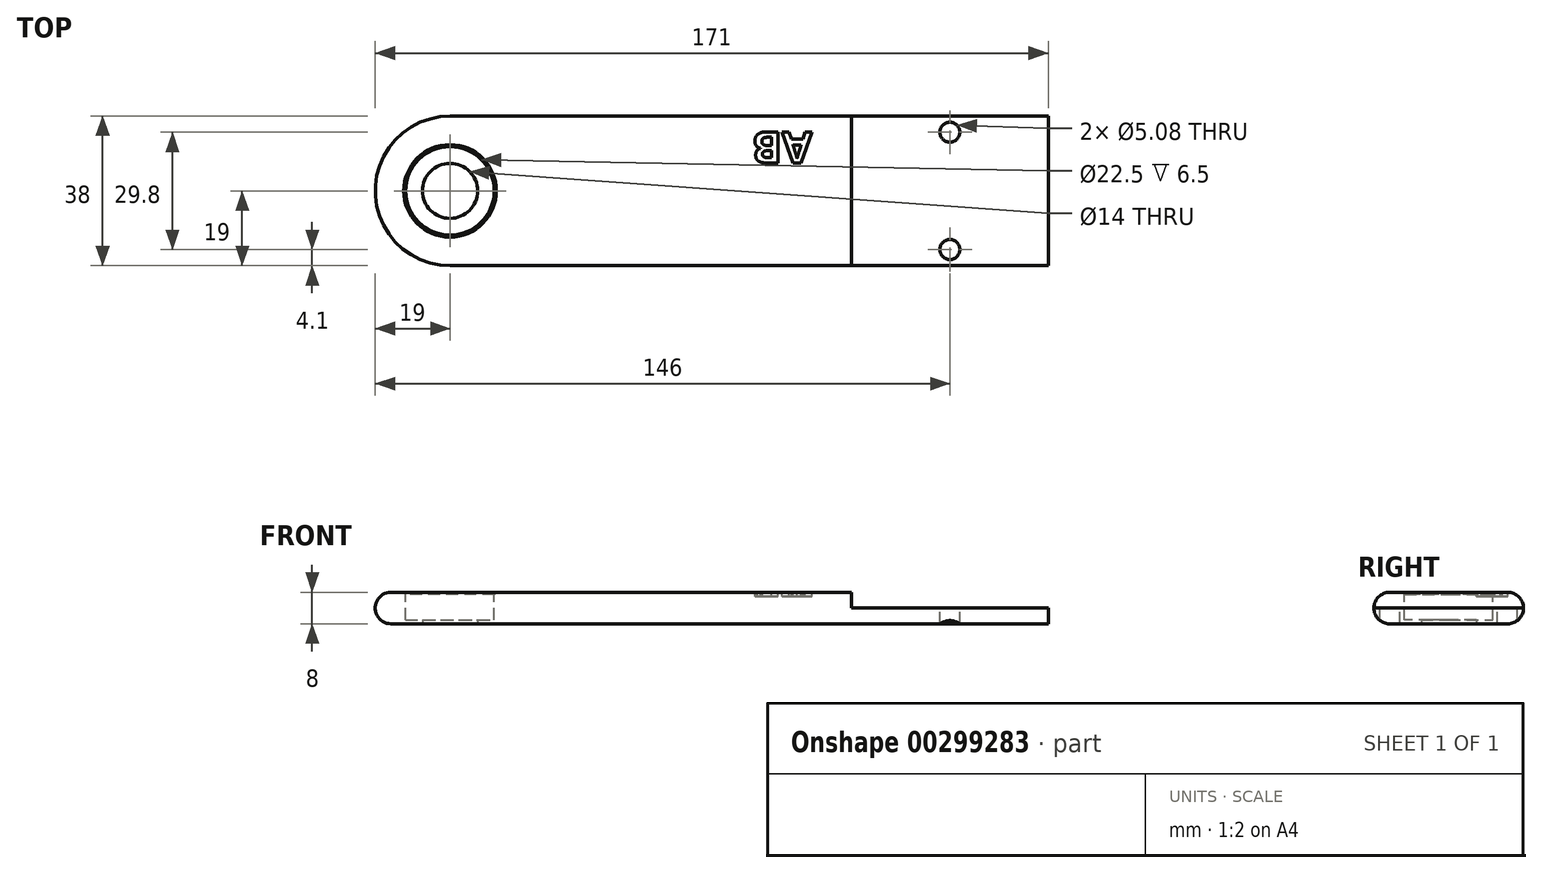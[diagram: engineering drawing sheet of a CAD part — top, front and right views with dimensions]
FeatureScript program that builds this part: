
annotation { "Feature Type Name" : "Feature", "Feature Type Description" : "" }
export const myFeature = defineFeature(function(context is Context, id is Id, definition is map)
    precondition{}
    {
        {
            var Q0;
            Q0=qCreatedBy(makeId("Top.planeOp"),FACE);
            var sketch = newSketch(context, id + "F0", { "sketchPlane" : qUnion([Q0])});
            skArc(sketch, "E0", {"start": v(-127, 19) * mm, "mid": v(-146, 0) * mm, "end": v(-127, -19) * mm});
            skArc(sketch, "E1", {"start": v(127, -19) * mm, "mid": v(146, 0) * mm, "end": v(127, 19) * mm});
            skCircle(sketch, "E2", {"center": v(-127, 0) * mm, "radius": 11.25 * mm});
            skCircle(sketch, "E3", {"center": v(127, 0) * mm, "radius": 11.25 * mm});
            skLineSegment(sketch, "E4", {"start": v(-127, 19) * mm, "end": v(127, 19) * mm});
            skLineSegment(sketch, "E5", {"start": v(-127, -19) * mm, "end": v(127, -19) * mm});
            skSolve(sketch);
        }
        {
            var Q0;
            Q0=makeQuery(id+"F0.imprint","IMPRINT",FACE,{"disambiguationData":[TD([[makeQuery(id+"F0.imprint","IMPRINT",EDGE,{"derivedFrom":sQuery(id+"F0.wireOp",EDGE,"E0")}),1.0]])]});
            var Q1;
            Q1=makeQuery(id+"F0.imprint","IMPRINT",FACE,{"disambiguationData":[TD([[makeQuery(id+"F0.imprint","IMPRINT",EDGE,{"derivedFrom":sQuery(id+"F0.wireOp",EDGE,"E3")}),1.0]])]});
            extrude(context, id + "F1", {"entities" : qUnion([Q0, Q1]), "oppositeDirection" : true, "depth" : 8 * mm});
        }
        {
            var Q0;
            Q0=makeQuery(id+"F1.opExtrude","CAP_FACE",FACE,{"disambiguationData":[OSD([sQuery(id+"F0.wireOp",EDGE,"E0"),sQuery(id+"F0.wireOp",EDGE,"E1"),sQuery(id+"F0.wireOp",EDGE,"E2"),sQuery(id+"F0.wireOp",EDGE,"E3"),sQuery(id+"F0.wireOp",EDGE,"E4"),sQuery(id+"F0.wireOp",EDGE,"E5")])],"isStart":false});
            var sketch = newSketch(context, id + "F2", { "sketchPlane" : qUnion([Q0])});
            skCircle(sketch, "E6", {"center": v(-127, 0) * mm, "radius": 7 * mm});
            skCircle(sketch, "E7.0", {"center": v(-127, 0) * mm, "radius": 11.25 * mm});
            skSolve(sketch);
        }
        {
            var Q0;
            Q0=makeQuery(id+"F2.imprint","IMPRINT",FACE,{"disambiguationData":[TD([[makeQuery(id+"F2.imprint","IMPRINT",EDGE,{"derivedFrom":sQuery(id+"F2.wireOp",EDGE,"E6")}),-1.0]])]});
            extrude(context, id + "F3", {"entities" : qUnion([Q0]), "operationType" : NewBodyOperationType.ADD, "oppositeDirection" : true, "depth" : 1 * mm});
        }
        {
            var Q0;
            Q0=qCreatedBy(makeId("Front.planeOp"),FACE);
            var sketch = newSketch(context, id + "F4", { "sketchPlane" : qUnion([Q0])});
            skLineSegment(sketch, "E8", {"start": v(127, -32) * mm, "end": v(127, 18) * mm, "construction": true});
            skLineSegment(sketch, "E9.bottom", {"start": v(129, -8) * mm, "end": v(131, -8) * mm});
            skLineSegment(sketch, "E9.top", {"start": v(129, -17.5) * mm, "end": v(131, -17.5) * mm});
            skLineSegment(sketch, "E9.left", {"start": v(129, -8) * mm, "end": v(129, -17.5) * mm});
            skLineSegment(sketch, "E9.right", {"start": v(131, -8) * mm, "end": v(131, -17.5) * mm});
            skLineSegment(sketch, "E10.bottom", {"start": v(131, -17.5) * mm, "end": v(132.5, -17.5) * mm});
            skLineSegment(sketch, "E10.top", {"start": v(131, -16) * mm, "end": v(132.5, -16) * mm});
            skLineSegment(sketch, "E10.left", {"start": v(131, -17.5) * mm, "end": v(131, -16) * mm});
            skLineSegment(sketch, "E10.right", {"start": v(133, -17) * mm, "end": v(133, -16.5) * mm});
            skPoint(sketch, "E11.visualSharp", {"position": v(133, -17.5) * mm});
            skArc(sketch, "E11.filletArc", {"start": v(132.5, -17.5) * mm, "mid": v(132.85, -17.35) * mm, "end": v(133, -17) * mm});
            skPoint(sketch, "E12.visualSharp", {"position": v(133, -16) * mm});
            skArc(sketch, "E12.filletArc", {"start": v(133, -16.5) * mm, "mid": v(132.85, -16.15) * mm, "end": v(132.5, -16) * mm});
            skSolve(sketch);
        }
        {
            var Q0;
            Q0=makeQuery(id+"F4.imprint","IMPRINT",FACE,{"disambiguationData":[TD([[makeQuery(id+"F4.imprint","IMPRINT",EDGE,{"derivedFrom":sQuery(id+"F4.wireOp",EDGE,"E9.bottom")}),-1.0]])]});
            var Q1;
            Q1=makeQuery(id+"F4.imprint","IMPRINT",FACE,{"disambiguationData":[TD([[makeQuery(id+"F4.imprint","IMPRINT",EDGE,{"derivedFrom":sQuery(id+"F4.wireOp",EDGE,"E10.bottom")}),1.0]])]});
            var Q2;
            Q2=sQuery(id+"F4.wireOp",EDGE,"E8");
            revolve(context, id + "F5", {"operationType" : NewBodyOperationType.ADD, "entities" : qUnion([Q0, Q1]), "axis" : qUnion([Q2]), "revolveType" : RevolveType.ONE_DIRECTION, "angle" : 90 * degree});
        }
        {
            var Q0;
            Q0=qCreatedBy(makeId("Front.planeOp"),FACE);
            var sketch = newSketch(context, id + "F6", { "sketchPlane" : qUnion([Q0])});
            skLineSegment(sketch, "E13", {"start": v(-25, -4) * mm, "end": v(25, -4) * mm});
            skLineSegment(sketch, "E14", {"start": v(-25, -4) * mm, "end": v(-25, 0) * mm});
            skLineSegment(sketch, "E15", {"start": v(25, -4) * mm, "end": v(25, -8) * mm});
            skLineSegment(sketch, "E16", {"start": v(25, -8) * mm, "end": v(152.55, -37.68) * mm});
            skLineSegment(sketch, "E17", {"start": v(152.55, -37.68) * mm, "end": v(152.55, 13.45) * mm});
            skLineSegment(sketch, "E18", {"start": v(152.55, 13.45) * mm, "end": v(-25, 0) * mm});
            skLineSegment(sketch, "E19", {"start": v(-25, 0) * mm, "end": v(-153.56, 12.9) * mm});
            skLineSegment(sketch, "E20", {"start": v(-153.56, 12.9) * mm, "end": v(-153.56, -26.79) * mm});
            skLineSegment(sketch, "E21", {"start": v(-153.56, -26.79) * mm, "end": v(25, -8) * mm});
            skSolve(sketch);
        }
        {
            var Q0;
            Q0=makeQuery(id+"F6.imprint","IMPRINT",FACE,{"disambiguationData":[TD([[makeQuery(id+"F6.imprint","IMPRINT",EDGE,{"derivedFrom":sQuery(id+"F6.wireOp",EDGE,"E13")}),1.0]])]});
            extrude(context, id + "F7", {"entities" : qUnion([Q0]), "operationType" : NewBodyOperationType.REMOVE, "endBound" : BoundingType.SYMMETRIC, "depth" : 42 * mm});
        }
        {
            var Q0;
            Q0=makeQuery(id+"F1.opExtrude","CAP_EDGE",EDGE,{"disambiguationData":[OSD([sQuery(id+"F0.wireOp",EDGE,"E5")])],"isStart":true});
            var Q1;
            Q1=makeQuery(id+"F1.opExtrude","CAP_EDGE",EDGE,{"disambiguationData":[OSD([sQuery(id+"F0.wireOp",EDGE,"E5")])],"isStart":false});
            fillet(context, id + "F8", {"entities" : qUnion([Q0, Q1]), "radius" : 4 * mm, "tangentPropagation" : true, "allowEdgeOverflow" : false});
        }
        {
            var Q0;
            Q0=makeQuery(id+"F7.boolean.opBoolean","COPY",FACE,{"derivedFrom":makeQuery(id+"F7.opExtrude","SWEPT_FACE",FACE,{"disambiguationData":[OSD([sQuery(id+"F6.wireOp",EDGE,"E13")])]})});
            var sketch = newSketch(context, id + "F9", { "sketchPlane" : qUnion([Q0])});
            skLineSegment(sketch, "E22", {"start": v(0, -14.9) * mm, "end": v(0, 14.9) * mm, "construction": true});
            skLineSegment(sketch, "E23", {"start": v(0, -14.9) * mm, "end": v(0, -19) * mm, "construction": true});
            skLineSegment(sketch, "E24", {"start": v(0, 14.9) * mm, "end": v(0, 19) * mm, "construction": true});
            skPoint(sketch, "E25", {"position": v(0, -14.9) * mm});
            skPoint(sketch, "E26", {"position": v(0, 14.9) * mm});
            skSolve(sketch);
        }
        {
            var Q0;
            Q0=sQuery(id+"F9.wireOp",VERTEX,"E26");
            var Q1;
            Q1=sQuery(id+"F9.wireOp",VERTEX,"E25");
            var Q2;
            Q2=makeQuery(id+"F1.opExtrude","SWEPT_BODY",BODY,{"disambiguationData":[OSD([sQuery(id+"F0.wireOp",EDGE,"E0"),sQuery(id+"F0.wireOp",EDGE,"E1"),sQuery(id+"F0.wireOp",EDGE,"E2"),sQuery(id+"F0.wireOp",EDGE,"E4"),sQuery(id+"F0.wireOp",EDGE,"E5")])]});
            hole(context, id + "F10", {"style" : HoleStyle.SIMPLE, "endStyle" : HoleEndStyle.THROUGH, "holeDiameter" : 5.08 * mm, "tappedDepth" : 12.7 * mm, "tapClearance" : 3, "locations" : qUnion([Q0, Q1]), "scope" : qUnion([Q2])});
        }
        {
            var Q0;
            Q0=makeQuery(id+"F1.opExtrude","CAP_FACE",FACE,{"disambiguationData":[OSD([sQuery(id+"F0.wireOp",EDGE,"E0"),sQuery(id+"F0.wireOp",EDGE,"E1"),sQuery(id+"F0.wireOp",EDGE,"E2"),sQuery(id+"F0.wireOp",EDGE,"E4"),sQuery(id+"F0.wireOp",EDGE,"E5")])],"isStart":true});
            var sketch = newSketch(context, id + "F11", { "sketchPlane" : qUnion([Q0])});
            skText(sketch, "E27", { "text": "AB", "fontName": "OpenSans-Bold.ttf"});
            const initialGuessF11  = {"E27": [-0.035, 0.015, -1, 0, 0.008]};
            skSetInitialGuess(sketch, initialGuessF11);
            skSolve(sketch);
        }
        {
            var Q0;
            Q0 = qSketchRegion(id + "F11", true);
            extrude(context, id + "F12", {"entities" : qUnion([Q0]), "operationType" : NewBodyOperationType.REMOVE, "oppositeDirection" : true, "depth" : 1 * mm});
        }
        {
            var Q0;
            Q0=makeQuery(id+"F1.opExtrude","CAP_EDGE",EDGE,{"disambiguationData":[OSD([sQuery(id+"F0.wireOp",EDGE,"E2")])],"isStart":true});
            chamfer(context, id + "F13", {"entities" : qUnion([Q0]), "width" : .5 * mm, "tangentPropagation" : true});
        }
    });
